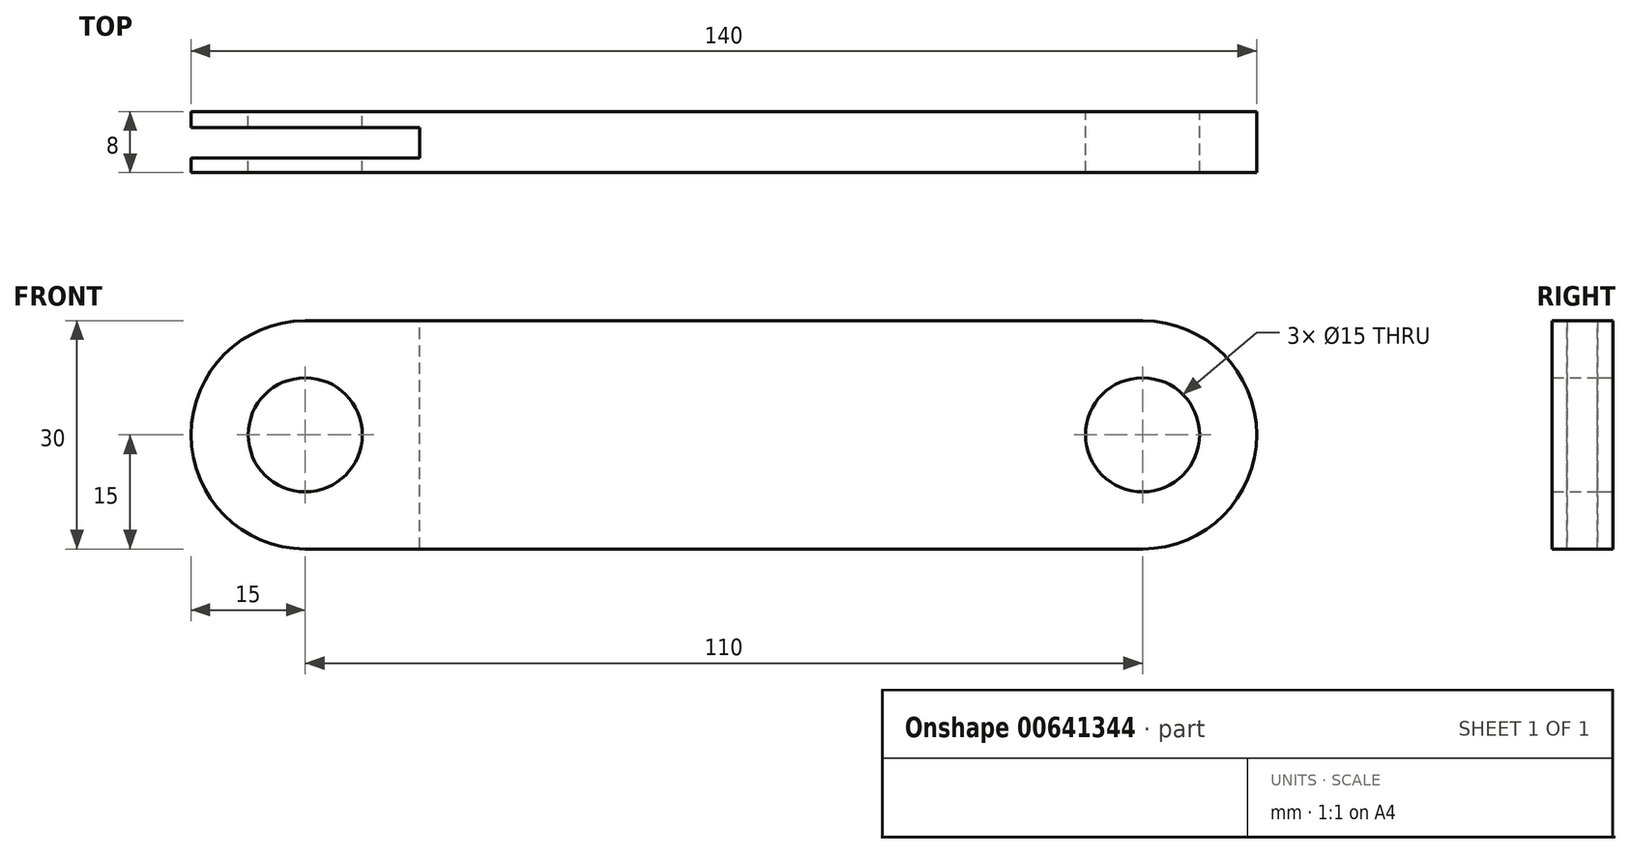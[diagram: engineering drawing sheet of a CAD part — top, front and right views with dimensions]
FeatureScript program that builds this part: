
annotation { "Feature Type Name" : "Feature", "Feature Type Description" : "" }
export const myFeature = defineFeature(function(context is Context, id is Id, definition is map)
    precondition{}
    {
        {
            var Q0;
            Q0=qCreatedBy(makeId("Front.planeOp"),FACE);
            var sketch = newSketch(context, id + "F0", { "sketchPlane" : qUnion([Q0])});
            skArc(sketch, "E0", {"start": v(0, 15) * mm, "mid": v(-15, 0) * mm, "end": v(0, -15) * mm});
            skArc(sketch, "E1", {"start": v(110, -15) * mm, "mid": v(125, 0) * mm, "end": v(110, 15) * mm});
            skLineSegment(sketch, "E2", {"start": v(0, 15) * mm, "end": v(110, 15) * mm});
            skLineSegment(sketch, "E3", {"start": v(0, -15) * mm, "end": v(110, -15) * mm});
            skSolve(sketch);
        }
        {
            var Q0;
            Q0=makeQuery(id+"F0.imprint","IMPRINT",FACE,{"disambiguationData":[TD([[makeQuery(id+"F0.imprint","IMPRINT",EDGE,{"derivedFrom":sQuery(id+"F0.wireOp",EDGE,"E0")}),1.0]])]});
            extrude(context, id + "F1", {"entities" : qUnion([Q0]), "depth" : 8 * mm, "offsetDistance" : 25 * mm});
        }
        {
            var Q0;
            Q0=sQuery(id+"F0.wireOp",VERTEX,"E0.center");
            var Q1;
            Q1=makeQuery(id+"F1.opExtrude","SWEPT_BODY",BODY,{"disambiguationData":[OSD([sQuery(id+"F0.wireOp",EDGE,"E0"),sQuery(id+"F0.wireOp",EDGE,"E1"),sQuery(id+"F0.wireOp",EDGE,"E2"),sQuery(id+"F0.wireOp",EDGE,"E3")])]});
            hole(context, id + "F2", {"style" : HoleStyle.SIMPLE, "endStyle" : HoleEndStyle.THROUGH, "oppositeDirection" : true, "standardTappedOrClearance" : lookupTablePath({ "fit" : "Normal", "standard" : "Custom", "size" : "M5", "type" : "Clearance" }), "standardBlindInLast" : lookupTablePath({ "fit" : "Standard", "standard" : "Custom", "size" : "M5", "type" : "Clearance" }), "holeDiameter" : 15 * mm, "majorDiameter" : 5 * mm, "isTappedThrough" : true, "tappedDepth" : 12 * mm, "tapClearance" : 3, "locations" : qUnion([Q0]), "scope" : qUnion([Q1])});
        }
        {
            var Q0;
            Q0=sQuery(id+"F0.wireOp",VERTEX,"E1.center");
            var Q1;
            Q1=makeQuery(id+"F1.opExtrude","SWEPT_BODY",BODY,{"disambiguationData":[OSD([sQuery(id+"F0.wireOp",EDGE,"E0"),sQuery(id+"F0.wireOp",EDGE,"E1"),sQuery(id+"F0.wireOp",EDGE,"E2"),sQuery(id+"F0.wireOp",EDGE,"E3")])]});
            hole(context, id + "F3", {"style" : HoleStyle.SIMPLE, "endStyle" : HoleEndStyle.THROUGH, "oppositeDirection" : true, "holeDiameter" : 15 * mm, "majorDiameter" : 5 * mm, "isTappedThrough" : true, "tappedDepth" : 12 * mm, "tapClearance" : 3, "locations" : qUnion([Q0]), "scope" : qUnion([Q1])});
        }
        {
            var Q0;
            Q0=qCreatedBy(makeId("Top.planeOp"),FACE);
            cPlane(context, id + "F4", {"entities" : qUnion([Q0]), "cplaneType" : CPlaneType.OFFSET, "offset" : 15 * mm, "width" : 150 * mm, "height" : 150 * mm});
        }
        {
            var Q0;
            Q0=qCreatedBy(id+"F4.planeOp",FACE);
            var sketch = newSketch(context, id + "F5", { "sketchPlane" : qUnion([Q0])});
            skLineSegment(sketch, "E4.bottom", {"start": v(-15, -2.06) * mm, "end": v(15, -2.06) * mm});
            skLineSegment(sketch, "E4.top", {"start": v(-15, -6.06) * mm, "end": v(15, -6.06) * mm});
            skLineSegment(sketch, "E4.left", {"start": v(-15, -2.06) * mm, "end": v(-15, -6.06) * mm});
            skLineSegment(sketch, "E4.right", {"start": v(15, -2.06) * mm, "end": v(15, -6.06) * mm});
            skSolve(sketch);
        }
        {
            var Q0;
            Q0=qSketchRegion(id+"F5",true);
            var Q1;
            Q1=qBodyType(qCreatedBy(id+"F5",EDGE),BodyType.WIRE);
            extrude(context, id + "F6", {"entities" : qUnion([Q0]), "operationType" : NewBodyOperationType.REMOVE, "surfaceEntities" : qUnion([Q1]), "endBound" : BoundingType.THROUGH_ALL, "oppositeDirection" : true, "depth" : 30 * mm, "offsetDistance" : 25 * mm});
        }
    });
